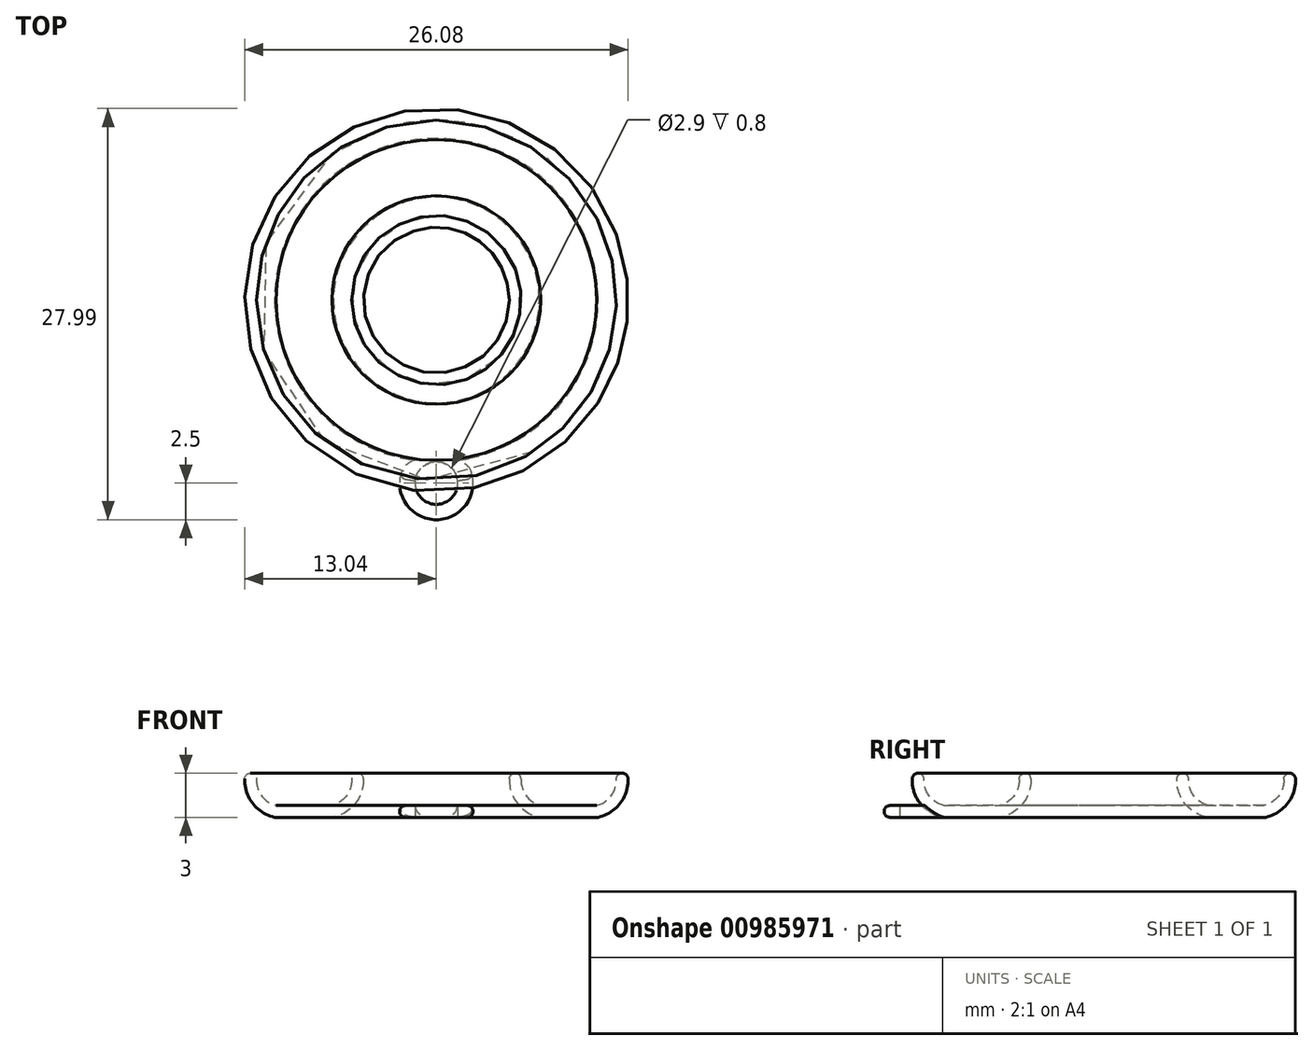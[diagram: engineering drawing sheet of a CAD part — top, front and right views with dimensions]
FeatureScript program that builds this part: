
annotation { "Feature Type Name" : "Feature", "Feature Type Description" : "" }
export const myFeature = defineFeature(function(context is Context, id is Id, definition is map)
    precondition{}
    {
        {
            var Q0;
            Q0=qCreatedBy(makeId("Front.planeOp"),FACE);
            var sketch = newSketch(context, id + "F0", { "sketchPlane" : qUnion([Q0])});
            skLineSegment(sketch, "E0", {"start": v(0, 21.94) * mm, "end": v(0, -25.46) * mm, "construction": true});
            skLineSegment(sketch, "E1", {"start": v(7, 0) * mm, "end": v(11, 0) * mm});
            skLineSegment(sketch, "E2", {"start": v(5, 3) * mm, "end": v(13, 3) * mm});
            skArc(sketch, "E3", {"start": v(5, 3) * mm, "mid": v(5.4, 1.1) * mm, "end": v(7, 0) * mm});
            skArc(sketch, "E4", {"start": v(11, 0) * mm, "mid": v(12.6, 1.1) * mm, "end": v(13, 3) * mm});
            skArc(sketch, "E5.0", {"start": v(10.9, 0.8) * mm, "mid": v(12, 1.64) * mm, "end": v(12.18, 3) * mm});
            skLineSegment(sketch, "E5.1", {"start": v(7.1, 0.8) * mm, "end": v(10.9, 0.8) * mm});
            skArc(sketch, "E5.2", {"start": v(5.82, 3) * mm, "mid": v(6, 1.64) * mm, "end": v(7.1, 0.8) * mm});
            skSolve(sketch);
        }
        {
            var Q0;
            Q0=makeQuery(id+"F0.imprint","IMPRINT",FACE,{"disambiguationData":[TD([[makeQuery(id+"F0.imprint","IMPRINT",EDGE,{"derivedFrom":sQuery(id+"F0.wireOp",EDGE,"E1")}),1.0]])]});
            var Q1;
            Q1=sQuery(id+"F0.wireOp",EDGE,"E0");
            revolve(context, id + "F1", {"surfaceOperationType" : NewSurfaceOperationType.NEW, "entities" : qUnion([Q0]), "axis" : qUnion([Q1]), "revolveType" : RevolveType.FULL});
        }
        {
            var Q0;
            Q0=makeQuery(id+"F1.opRevolve","SWEPT_EDGE",EDGE,{"disambiguationData":[OSD([sQuery(id+"F0.wireOp",EDGE,"E2"),sQuery(id+"F0.wireOp",EDGE,"E5.0")])]});
            var Q1;
            Q1=makeQuery(id+"F1.opRevolve","SWEPT_EDGE",EDGE,{"disambiguationData":[OSD([sQuery(id+"F0.wireOp",EDGE,"E2"),sQuery(id+"F0.wireOp",EDGE,"E5.2")])]});
            var Q2;
            Q2=makeQuery(id+"F1.opRevolve","SWEPT_EDGE",EDGE,{"disambiguationData":[OSD([sQuery(id+"F0.wireOp",EDGE,"E2"),sQuery(id+"F0.wireOp",EDGE,"E3")])]});
            var Q3;
            Q3=makeQuery(id+"F1.opRevolve","SWEPT_EDGE",EDGE,{"disambiguationData":[OSD([sQuery(id+"F0.wireOp",EDGE,"E2"),sQuery(id+"F0.wireOp",EDGE,"E4")])]});
            fillet(context, id + "F2", {"entities" : qUnion([Q0, Q1, Q2, Q3]), "radius" : .4 * mm, "tangentPropagation" : true, "allowEdgeOverflow" : false});
        }
        {
            var Q0;
            Q0=qCreatedBy(makeId("Top.planeOp"),FACE);
            var sketch = newSketch(context, id + "F3", { "sketchPlane" : qUnion([Q0])});
            skCircle(sketch, "E6", {"center": v(0, -12.45) * mm, "radius": 2.5 * mm});
            skCircle(sketch, "E7", {"center": v(0, -12.45) * mm, "radius": 1.45 * mm});
            skSolve(sketch);
        }
        {
            var Q0;
            Q0=makeQuery(id+"F3.imprint","IMPRINT",FACE,{"disambiguationData":[TD([[makeQuery(id+"F3.imprint","IMPRINT",EDGE,{"derivedFrom":sQuery(id+"F3.wireOp",EDGE,"E6")}),1.0]])]});
            extrude(context, id + "F4", {"entities" : qUnion([Q0]), "operationType" : NewBodyOperationType.ADD, "depth" : .8 * mm, "offsetDistance" : 25 * mm});
        }
        {
            var Q0;
            Q0=makeQuery(id+"F4.opExtrude","CAP_EDGE",EDGE,{"disambiguationData":[OSD([sQuery(id+"F3.wireOp",EDGE,"E6")])],"isStart":false});
            var Q1;
            Q1=makeQuery(id+"F4.opExtrude","CAP_EDGE",EDGE,{"disambiguationData":[OSD([sQuery(id+"F3.wireOp",EDGE,"E6")])],"isStart":true});
            fillet(context, id + "F5", {"entities" : qUnion([Q0, Q1]), "radius" : .4 * mm, "tangentPropagation" : true, "allowEdgeOverflow" : false});
        }
    });
